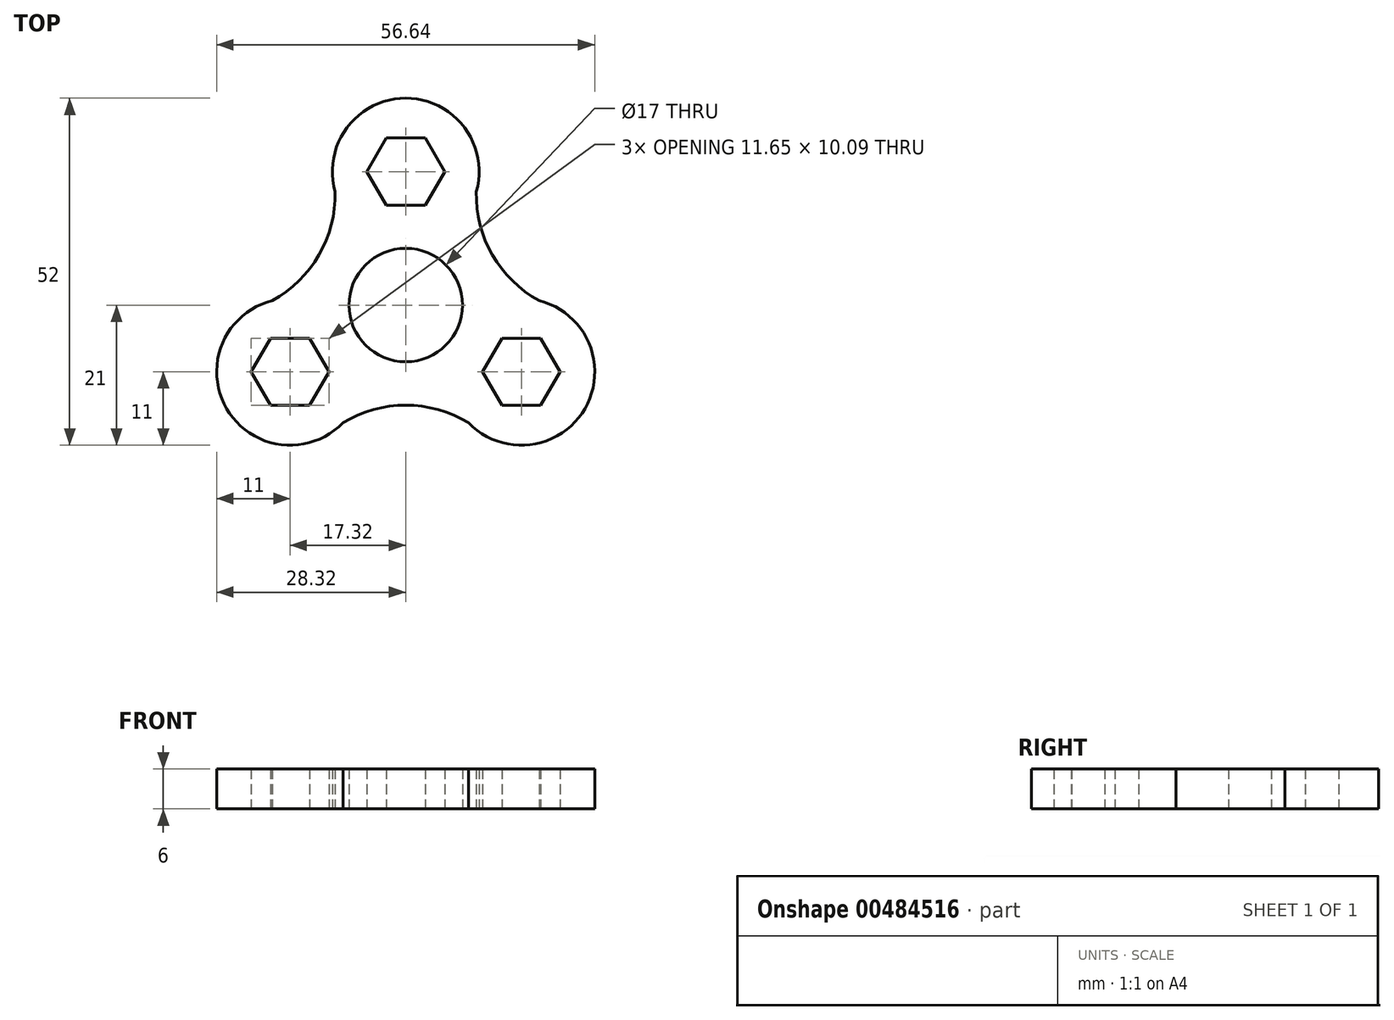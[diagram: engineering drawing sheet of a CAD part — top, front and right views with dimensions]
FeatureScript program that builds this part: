
annotation { "Feature Type Name" : "Feature", "Feature Type Description" : "" }
export const myFeature = defineFeature(function(context is Context, id is Id, definition is map)
    precondition{}
    {
        {
            var Q0;
            Q0=qCreatedBy(makeId("Top.planeOp"),FACE);
            var sketch = newSketch(context, id + "F0", { "sketchPlane" : qUnion([Q0])});
            skCircle(sketch, "E0", {"center": v(0, 0) * mm, "radius": 8.5 * mm});
            skCircle(sketch, "E1", {"center": v(0, 0) * mm, "radius": 15 * mm, "construction": true});
            skCircle(sketch, "E2", {"center": v(0, 0) * mm, "radius": 20 * mm, "construction": true});
            skArc(sketch, "E3", {"start": v(-10.58, 16.98) * mm, "mid": v(0, 31) * mm, "end": v(10.58, 16.98) * mm});
            skArc(sketch, "E4.1.1", {"start": v(-9.41, -17.65) * mm, "mid": v(-26.85, -15.5) * mm, "end": v(-19.99, 0.67) * mm});
            skArc(sketch, "E4.2.1", {"start": v(19.99, 0.67) * mm, "mid": v(26.85, -15.5) * mm, "end": v(9.41, -17.65) * mm});
            skArc(sketch, "E5", {"start": v(-19.99, 0.67) * mm, "mid": v(-13, 7.5) * mm, "end": v(-10.58, 16.97) * mm});
            skArc(sketch, "E6", {"start": v(9.41, -17.65) * mm, "mid": v(0, -15) * mm, "end": v(-9.41, -17.65) * mm});
            skArc(sketch, "E7", {"start": v(10.58, 16.97) * mm, "mid": v(13, 7.5) * mm, "end": v(19.99, 0.67) * mm});
            skCircle(sketch, "E8.cCircle", {"center": v(0, 20) * mm, "radius": 5.04 * mm, "construction": true});
            skLineSegment(sketch, "E8.0", {"start": v(-2.91, 25.05) * mm, "end": v(2.91, 25.05) * mm});
            skLineSegment(sketch, "E8.1", {"start": v(2.91, 25.05) * mm, "end": v(5.83, 20) * mm});
            skLineSegment(sketch, "E8.2", {"start": v(5.83, 20) * mm, "end": v(2.91, 14.96) * mm});
            skLineSegment(sketch, "E8.3", {"start": v(2.91, 14.96) * mm, "end": v(-2.91, 14.96) * mm});
            skLineSegment(sketch, "E8.4", {"start": v(-2.91, 14.96) * mm, "end": v(-5.83, 20) * mm});
            skLineSegment(sketch, "E8.5", {"start": v(-5.83, 20) * mm, "end": v(-2.91, 25.05) * mm});
            skPoint(sketch, "E8.0.midPoint", {"position": v(0, 25.05) * mm});
            skLineSegment(sketch, "E9.1.0", {"start": v(-14.4, -15.04) * mm, "end": v(-20.23, -15.04) * mm});
            skLineSegment(sketch, "E9.1.1", {"start": v(-20.23, -15.05) * mm, "end": v(-23.15, -10) * mm});
            skLineSegment(sketch, "E9.1.2", {"start": v(-23.15, -10) * mm, "end": v(-20.23, -4.95) * mm});
            skLineSegment(sketch, "E9.1.3", {"start": v(-20.23, -4.95) * mm, "end": v(-14.4, -4.95) * mm});
            skLineSegment(sketch, "E9.1.4", {"start": v(-14.4, -4.95) * mm, "end": v(-11.5, -10) * mm});
            skLineSegment(sketch, "E9.1.5", {"start": v(-11.5, -10) * mm, "end": v(-14.4, -15.04) * mm});
            skLineSegment(sketch, "E9.2.0", {"start": v(20.23, -4.95) * mm, "end": v(23.15, -10) * mm});
            skLineSegment(sketch, "E9.2.1", {"start": v(23.15, -10) * mm, "end": v(20.23, -15.04) * mm});
            skLineSegment(sketch, "E9.2.2", {"start": v(20.23, -15.04) * mm, "end": v(14.4, -15.05) * mm});
            skLineSegment(sketch, "E9.2.3", {"start": v(14.4, -15.05) * mm, "end": v(11.5, -10) * mm});
            skLineSegment(sketch, "E9.2.4", {"start": v(11.5, -10) * mm, "end": v(14.4, -4.95) * mm});
            skLineSegment(sketch, "E9.2.5", {"start": v(14.4, -4.96) * mm, "end": v(20.23, -4.95) * mm});
            skSolve(sketch);
        }
        {
            var Q0;
            Q0=makeQuery(id+"F0.imprint","IMPRINT",FACE,{"disambiguationData":[TD([[makeQuery(id+"F0.imprint","IMPRINT",EDGE,{"derivedFrom":sQuery(id+"F0.wireOp",EDGE,"E0")}),-1.0]])]});
            extrude(context, id + "F1", {"entities" : qUnion([Q0]), "depth" : 6 * mm});
        }
    });
